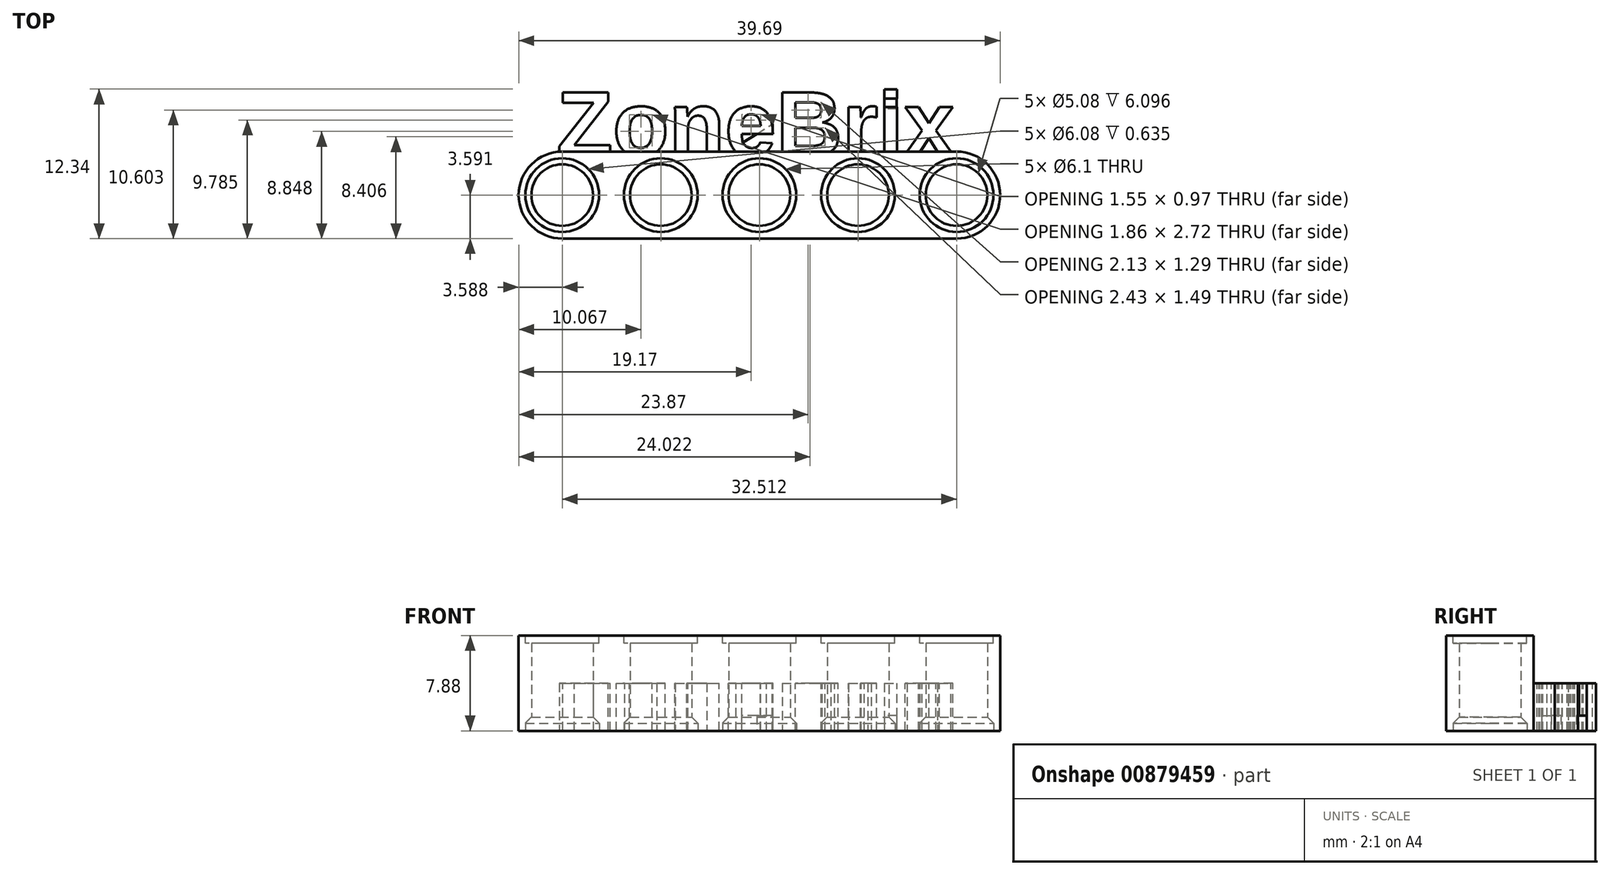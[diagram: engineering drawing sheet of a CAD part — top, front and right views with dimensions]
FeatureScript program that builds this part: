
annotation { "Feature Type Name" : "Feature", "Feature Type Description" : "" }
export const myFeature = defineFeature(function(context is Context, id is Id, definition is map)
    precondition{}
    {
        {
            var Q0;
            Q0=qCreatedBy(makeId("Top.planeOp"),FACE);
            var sketch = newSketch(context, id + "F0", { "sketchPlane" : qUnion([Q0])});
            skCircle(sketch, "E0", {"center": v(-60.84, 14.37) * mm, "radius": 3.6 * mm});
            skCircle(sketch, "E1.1.0.0", {"center": v(-52.71, 14.37) * mm, "radius": 3.6 * mm});
            skCircle(sketch, "E1.2.0.0", {"center": v(-44.59, 14.37) * mm, "radius": 3.6 * mm});
            skCircle(sketch, "E1.3.0.0", {"center": v(-36.46, 14.37) * mm, "radius": 3.6 * mm});
            skLineSegment(sketch, "E1.direction1", {"start": v(-60.84, 14.37) * mm, "end": v(-52.71, 14.37) * mm, "construction": true});
            skCircle(sketch, "E2.0.4.0", {"center": v(-28.33, 14.37) * mm, "radius": 3.6 * mm});
            skLineSegment(sketch, "E3.left", {"start": v(-60.84, 14.37) * mm, "end": v(-60.84, 14.37) * mm});
            skLineSegment(sketch, "E3.right", {"start": v(-28.33, 14.37) * mm, "end": v(-28.33, 14.37) * mm});
            skLineSegment(sketch, "E4.bottom", {"start": v(-60.84, 17.96) * mm, "end": v(-28.33, 17.96) * mm});
            skLineSegment(sketch, "E4.top", {"start": v(-60.84, 10.78) * mm, "end": v(-28.33, 10.78) * mm});
            skCircle(sketch, "E5", {"center": v(-60.84, 14.37) * mm, "radius": 3.05 * mm});
            skCircle(sketch, "E6.1.0.0", {"center": v(-52.71, 14.37) * mm, "radius": 3.05 * mm});
            skCircle(sketch, "E6.2.0.0", {"center": v(-44.59, 14.37) * mm, "radius": 3.05 * mm});
            skCircle(sketch, "E6.3.0.0", {"center": v(-36.46, 14.37) * mm, "radius": 3.05 * mm});
            skCircle(sketch, "E6.4.0.0", {"center": v(-28.33, 14.37) * mm, "radius": 3.05 * mm});
            skCircle(sketch, "E7", {"center": v(-60.84, 14.37) * mm, "radius": 2.54 * mm});
            skCircle(sketch, "E8.1.0.0", {"center": v(-52.71, 14.37) * mm, "radius": 2.54 * mm});
            skCircle(sketch, "E8.2.0.0", {"center": v(-44.59, 14.37) * mm, "radius": 2.54 * mm});
            skCircle(sketch, "E8.3.0.0", {"center": v(-36.46, 14.37) * mm, "radius": 2.54 * mm});
            skCircle(sketch, "E8.4.0.0", {"center": v(-28.33, 14.37) * mm, "radius": 2.54 * mm});
            skSolve(sketch);
        }
        {
            var Q0;
            Q0=makeQuery(id+"F0.imprint","IMPRINT",FACE,{"disambiguationData":[TD([[makeQuery(id+"F0.imprint","IMPRINT",EDGE,{"derivedFrom":sQuery(id+"F0.wireOp",EDGE,"E6.2.0.0")}),1.0]])]});
            var Q1;
            {var subQ0=sQuery(id+"F0.wireOp",EDGE,"E4.bottom");var subQ1=sQuery(id+"F0.wireOp",EDGE,"E0");var subQ2=makeQuery(id+"F0.imprint","INTERSECT",VERTEX,{"derivedFrom":[subQ1,subQ0]});Q1=makeQuery(id+"F0.imprint","IMPRINT",FACE,{"disambiguationData":[TD([[makeQuery(id+"F0.imprint","IMPRINT",EDGE,{"disambiguationData":[TD([[subQ2,1.0]])],"derivedFrom":subQ1}),-1.0]])]});}
            var Q2;
            {var subQ0=sQuery(id+"F0.wireOp",EDGE,"E4.bottom");var subQ1=sQuery(id+"F0.wireOp",EDGE,"E1.1.0.0");var subQ2=makeQuery(id+"F0.imprint","INTERSECT",VERTEX,{"derivedFrom":[subQ1,subQ0]});Q2=makeQuery(id+"F0.imprint","IMPRINT",FACE,{"disambiguationData":[TD([[makeQuery(id+"F0.imprint","IMPRINT",EDGE,{"disambiguationData":[TD([[subQ2,1.0]])],"derivedFrom":subQ1}),-1.0]])]});}
            var Q3;
            Q3=makeQuery(id+"F0.imprint","IMPRINT",FACE,{"disambiguationData":[TD([[makeQuery(id+"F0.imprint","IMPRINT",EDGE,{"derivedFrom":sQuery(id+"F0.wireOp",EDGE,"E6.2.0.0")}),-1.0]])]});
            var Q4;
            Q4=makeQuery(id+"F0.imprint","IMPRINT",FACE,{"disambiguationData":[TD([[makeQuery(id+"F0.imprint","IMPRINT",EDGE,{"derivedFrom":sQuery(id+"F0.wireOp",EDGE,"E6.1.0.0")}),-1.0]])]});
            var Q5;
            Q5=makeQuery(id+"F0.imprint","IMPRINT",FACE,{"disambiguationData":[TD([[makeQuery(id+"F0.imprint","IMPRINT",EDGE,{"derivedFrom":sQuery(id+"F0.wireOp",EDGE,"E6.3.0.0")}),-1.0]])]});
            var Q6;
            Q6=makeQuery(id+"F0.imprint","IMPRINT",FACE,{"disambiguationData":[TD([[makeQuery(id+"F0.imprint","IMPRINT",EDGE,{"derivedFrom":sQuery(id+"F0.wireOp",EDGE,"E6.3.0.0")}),1.0]])]});
            var Q7;
            {var subQ0=sQuery(id+"F0.wireOp",EDGE,"E4.bottom");var subQ1=sQuery(id+"F0.wireOp",EDGE,"E1.3.0.0");var subQ2=makeQuery(id+"F0.imprint","INTERSECT",VERTEX,{"derivedFrom":[subQ1,subQ0]});Q7=makeQuery(id+"F0.imprint","IMPRINT",FACE,{"disambiguationData":[TD([[makeQuery(id+"F0.imprint","IMPRINT",EDGE,{"disambiguationData":[TD([[subQ2,1.0]])],"derivedFrom":subQ1}),-1.0]])]});}
            var Q8;
            Q8=makeQuery(id+"F0.imprint","IMPRINT",FACE,{"disambiguationData":[TD([[makeQuery(id+"F0.imprint","IMPRINT",EDGE,{"derivedFrom":sQuery(id+"F0.wireOp",EDGE,"E6.4.0.0")}),-1.0]])]});
            var Q9;
            Q9=makeQuery(id+"F0.imprint","IMPRINT",FACE,{"disambiguationData":[TD([[makeQuery(id+"F0.imprint","IMPRINT",EDGE,{"derivedFrom":sQuery(id+"F0.wireOp",EDGE,"E6.1.0.0")}),1.0]])]});
            var Q10;
            {var subQ0=sQuery(id+"F0.wireOp",EDGE,"E4.bottom");var subQ1=sQuery(id+"F0.wireOp",EDGE,"E1.2.0.0");var subQ2=makeQuery(id+"F0.imprint","INTERSECT",VERTEX,{"derivedFrom":[subQ1,subQ0]});Q10=makeQuery(id+"F0.imprint","IMPRINT",FACE,{"disambiguationData":[TD([[makeQuery(id+"F0.imprint","IMPRINT",EDGE,{"disambiguationData":[TD([[subQ2,1.0]])],"derivedFrom":subQ1}),-1.0]])]});}
            var Q11;
            Q11=makeQuery(id+"F0.imprint","IMPRINT",FACE,{"disambiguationData":[TD([[makeQuery(id+"F0.imprint","IMPRINT",EDGE,{"derivedFrom":sQuery(id+"F0.wireOp",EDGE,"E6.4.0.0")}),1.0]])]});
            var Q12;
            Q12=makeQuery(id+"F0.imprint","IMPRINT",FACE,{"disambiguationData":[TD([[makeQuery(id+"F0.imprint","IMPRINT",EDGE,{"derivedFrom":sQuery(id+"F0.wireOp",EDGE,"E5")}),-1.0]])]});
            var Q13;
            Q13=makeQuery(id+"F0.imprint","IMPRINT",FACE,{"disambiguationData":[TD([[makeQuery(id+"F0.imprint","IMPRINT",EDGE,{"derivedFrom":sQuery(id+"F0.wireOp",EDGE,"E5")}),1.0]])]});
            extrude(context, id + "F1", {"entities" : qUnion([Q0, Q1, Q2, Q3, Q4, Q5, Q6, Q7, Q8, Q9, Q10, Q11, Q12, Q13]), "endBound" : BoundingType.SYMMETRIC, "depth" : 7.87 * mm});
        }
        {
            var Q0;
            Q0=makeQuery(id+"F1.opExtrude","CAP_FACE",FACE,{"disambiguationData":[OSD([sQuery(id+"F0.wireOp",EDGE,"E0"),sQuery(id+"F0.wireOp",EDGE,"E2.0.4.0"),sQuery(id+"F0.wireOp",EDGE,"E4.bottom"),sQuery(id+"F0.wireOp",EDGE,"E4.top"),sQuery(id+"F0.wireOp",EDGE,"E7"),sQuery(id+"F0.wireOp",EDGE,"E8.1.0.0"),sQuery(id+"F0.wireOp",EDGE,"E8.2.0.0"),sQuery(id+"F0.wireOp",EDGE,"E8.3.0.0"),sQuery(id+"F0.wireOp",EDGE,"E8.4.0.0")])],"isStart":false});
            var sketch = newSketch(context, id + "F2", { "sketchPlane" : qUnion([Q0])});
            skCircle(sketch, "E9", {"center": v(-28.33, 14.37) * mm, "radius": 3.04 * mm});
            skCircle(sketch, "E10.1.0.0", {"center": v(-36.46, 14.37) * mm, "radius": 3.04 * mm});
            skCircle(sketch, "E10.2.0.0", {"center": v(-44.59, 14.37) * mm, "radius": 3.04 * mm});
            skCircle(sketch, "E10.3.0.0", {"center": v(-52.71, 14.37) * mm, "radius": 3.04 * mm});
            skCircle(sketch, "E10.4.0.0", {"center": v(-60.84, 14.37) * mm, "radius": 3.04 * mm});
            skLineSegment(sketch, "E10.direction1", {"start": v(-28.33, 14.37) * mm, "end": v(-36.46, 14.37) * mm, "construction": true});
            skSolve(sketch);
        }
        {
            var Q0;
            Q0=qSketchRegion(id+"F2",true);
            extrude(context, id + "F3", {"entities" : qUnion([Q0]), "operationType" : NewBodyOperationType.REMOVE, "oppositeDirection" : true, "depth" : 0.64 * mm});
        }
        {
            var Q0;
            Q0=makeQuery(id+"F1.opExtrude","CAP_FACE",FACE,{"disambiguationData":[OSD([sQuery(id+"F0.wireOp",EDGE,"E0"),sQuery(id+"F0.wireOp",EDGE,"E2.0.4.0"),sQuery(id+"F0.wireOp",EDGE,"E4.bottom"),sQuery(id+"F0.wireOp",EDGE,"E4.top"),sQuery(id+"F0.wireOp",EDGE,"E7"),sQuery(id+"F0.wireOp",EDGE,"E8.1.0.0"),sQuery(id+"F0.wireOp",EDGE,"E8.2.0.0"),sQuery(id+"F0.wireOp",EDGE,"E8.3.0.0"),sQuery(id+"F0.wireOp",EDGE,"E8.4.0.0")])],"isStart":true});
            var sketch = newSketch(context, id + "F4", { "sketchPlane" : qUnion([Q0])});
            skCircle(sketch, "E11", {"center": v(-60.84, -14.37) * mm, "radius": 3.05 * mm});
            skCircle(sketch, "E12.1.0.0", {"center": v(-52.71, -14.37) * mm, "radius": 3.05 * mm});
            skCircle(sketch, "E12.2.0.0", {"center": v(-44.59, -14.37) * mm, "radius": 3.05 * mm});
            skCircle(sketch, "E12.3.0.0", {"center": v(-36.46, -14.37) * mm, "radius": 3.05 * mm});
            skCircle(sketch, "E12.4.0.0", {"center": v(-28.33, -14.37) * mm, "radius": 3.05 * mm});
            skLineSegment(sketch, "E12.direction1", {"start": v(-60.84, -14.37) * mm, "end": v(-52.71, -14.37) * mm, "construction": true});
            skSolve(sketch);
        }
        {
            var Q0;
            Q0=qSketchRegion(id+"F4",true);
            extrude(context, id + "F5", {"entities" : qUnion([Q0]), "operationType" : NewBodyOperationType.REMOVE, "oppositeDirection" : true, "depth" : 0.64 * mm});
        }
        {
            var Q0;
            Q0=qCreatedBy(makeId("Top.planeOp"),FACE);
            var sketch = newSketch(context, id + "F6", { "sketchPlane" : qUnion([Q0])});
            skText(sketch, "E13", { "text": "ZoneBrix", "fontName": "Arimo-Bold.ttf"});
            const initialGuessF6  = {"E13": [-0.0613, 0.01763, 1, 0, 0.00545]};
            skSetInitialGuess(sketch, initialGuessF6);
            skSolve(sketch);
        }
        {
            var Q0;
            Q0=qSketchRegion(id+"F6",true);
            extrude(context, id + "F7", {"entities" : qUnion([Q0]), "operationType" : NewBodyOperationType.ADD, "oppositeDirection" : true, "offsetDistance" : 25.4 * mm, "depth" : 3.94 * mm});
        }
        {
            var Q0;
            Q0=makeQuery(id+"F5.boolean.opBoolean","INTERSECT",EDGE,{"derivedFrom":[makeQuery(id+"F1.opExtrude","SWEPT_FACE",FACE,{"disambiguationData":[OSD([sQuery(id+"F0.wireOp",EDGE,"E8.3.0.0")])]}),makeQuery(id+"F5.opExtrude","CAP_FACE",FACE,{"disambiguationData":[OSD([sQuery(id+"F4.wireOp",EDGE,"E12.3.0.0")])],"isStart":false})]});
            chamfer(context, id + "F8", {"entities" : qUnion([Q0]), "chamferType" : ChamferType.OFFSET_ANGLE, "width" : 0.5 * mm, "oppositeDirection" : false, "angle" : 45 * degree});
        }
        {
            var Q0;
            Q0=makeQuery(id+"F5.boolean.opBoolean","INTERSECT",EDGE,{"derivedFrom":[makeQuery(id+"F1.opExtrude","SWEPT_FACE",FACE,{"disambiguationData":[OSD([sQuery(id+"F0.wireOp",EDGE,"E8.2.0.0")])]}),makeQuery(id+"F5.opExtrude","CAP_FACE",FACE,{"disambiguationData":[OSD([sQuery(id+"F4.wireOp",EDGE,"E12.2.0.0")])],"isStart":false})]});
            var Q1;
            Q1=makeQuery(id+"F5.boolean.opBoolean","INTERSECT",EDGE,{"derivedFrom":[makeQuery(id+"F1.opExtrude","SWEPT_FACE",FACE,{"disambiguationData":[OSD([sQuery(id+"F0.wireOp",EDGE,"E8.1.0.0")])]}),makeQuery(id+"F5.opExtrude","CAP_FACE",FACE,{"disambiguationData":[OSD([sQuery(id+"F4.wireOp",EDGE,"E12.1.0.0")])],"isStart":false})]});
            var Q2;
            Q2=makeQuery(id+"F5.boolean.opBoolean","INTERSECT",EDGE,{"derivedFrom":[makeQuery(id+"F1.opExtrude","SWEPT_FACE",FACE,{"disambiguationData":[OSD([sQuery(id+"F0.wireOp",EDGE,"E7")])]}),makeQuery(id+"F5.opExtrude","CAP_FACE",FACE,{"disambiguationData":[OSD([sQuery(id+"F4.wireOp",EDGE,"E11")])],"isStart":false})]});
            var Q3;
            Q3=makeQuery(id+"F5.boolean.opBoolean","INTERSECT",EDGE,{"derivedFrom":[makeQuery(id+"F1.opExtrude","SWEPT_FACE",FACE,{"disambiguationData":[OSD([sQuery(id+"F0.wireOp",EDGE,"E8.4.0.0")])]}),makeQuery(id+"F5.opExtrude","CAP_FACE",FACE,{"disambiguationData":[OSD([sQuery(id+"F4.wireOp",EDGE,"E12.4.0.0")])],"isStart":false})]});
            chamfer(context, id + "F9", {"entities" : qUnion([Q0, Q1, Q2, Q3]), "chamferType" : ChamferType.OFFSET_ANGLE, "width" : 0.5 * mm, "oppositeDirection" : false, "angle" : 45 * degree});
        }
        {
            var Q0;
            Q0=makeQuery(id+"F7.opExtrude","CAP_FACE",FACE,{"disambiguationData":[OSD([sQuery(id+"F6.wireOp",EDGE,"E13.sketch_text.stroke-102"),sQuery(id+"F6.wireOp",EDGE,"E13.sketch_text.stroke-103"),sQuery(id+"F6.wireOp",EDGE,"E13.sketch_text.stroke-104"),sQuery(id+"F6.wireOp",EDGE,"E13.sketch_text.stroke-105")])],"isStart":false});
            var sketch = newSketch(context, id + "F10", { "sketchPlane" : qUnion([Q0])});
            skLineSegment(sketch, "E14.bottom", {"start": v(-33.26, -22.35) * mm, "end": v(-34.3, -22.35) * mm});
            skLineSegment(sketch, "E14.top", {"start": v(-33.26, -21.5) * mm, "end": v(-34.3, -21.5) * mm});
            skLineSegment(sketch, "E14.left", {"start": v(-33.26, -22.35) * mm, "end": v(-33.26, -21.5) * mm});
            skLineSegment(sketch, "E14.right", {"start": v(-34.3, -22.35) * mm, "end": v(-34.3, -21.5) * mm});
            skLineSegment(sketch, "E15", {"start": v(-43.5, -20.24) * mm, "end": v(-43.5, -19.43) * mm});
            skLineSegment(sketch, "E16", {"start": v(-43.5, -19.43) * mm, "end": v(-46.06, -19.43) * mm});
            skLineSegment(sketch, "E17", {"start": v(-46.06, -19.43) * mm, "end": v(-46.06, -18.65) * mm});
            skLineSegment(sketch, "E18", {"start": v(-46.06, -18.65) * mm, "end": v(-43.5, -20.24) * mm});
            skSolve(sketch);
        }
        {
            var Q0;
            Q0 = qSketchRegion(id + "F10", true);
            extrude(context, id + "F11", {"entities" : qUnion([Q0]), "oppositeDirection" : true, "depth" : 1.27 * mm, "offsetDistance" : 25.4 * mm});
        }
        {
            var Q0;
            Q0 = qSketchRegion(id + "F10", true);
            extrude(context, id + "F12", {"entities" : qUnion([Q0]), "oppositeDirection" : true, "depth" : 1.27 * mm, "offsetDistance" : 25.4 * mm});
        }
    });
